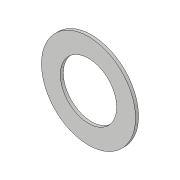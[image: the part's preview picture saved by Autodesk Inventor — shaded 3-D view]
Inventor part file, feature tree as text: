
AUTODESK INVENTOR PART (.ipt)
format: ipt  version: 2018.3 (Build 223284000, 284)  size: 79,872 bytes
history: native  units: in
note: dims shown in document units (in); Inventor stores cm internally (conversion verified against a paired STEP export)
features: extrude x1, sketch x1
ambient origin geometry x8: Origin, YZ Plane, XZ Plane, XY Plane, X Axis, Y Axis, Z Axis, Center Point
bodies: Solid1 (feature_tree)
feature tree (2):
  extrude  "Extrusion1"  Depth=0.02in
  sketch  "Sketch1"  dims[d0=0.375in d1=0.125in d2=0.02in d3=0.0in]
